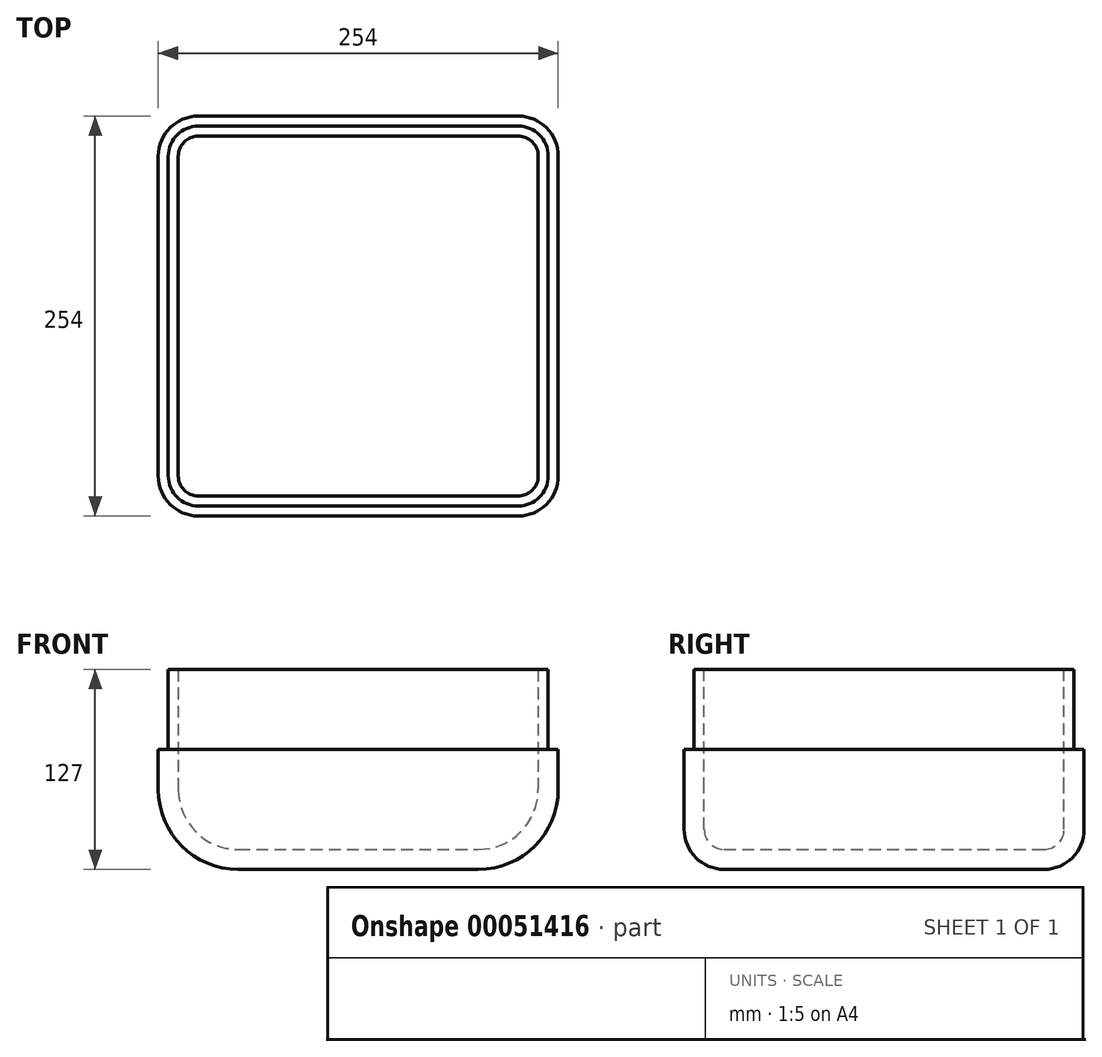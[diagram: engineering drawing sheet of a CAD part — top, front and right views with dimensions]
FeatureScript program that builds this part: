
annotation { "Feature Type Name" : "Feature", "Feature Type Description" : "" }
export const myFeature = defineFeature(function(context is Context, id is Id, definition is map)
    precondition{}
    {
        {
            var Q0;
            Q0=qCreatedBy(makeId("Top.planeOp"),FACE);
            var sketch = newSketch(context, id + "F0", { "sketchPlane" : qUnion([Q0])});
            skLineSegment(sketch, "E0.rect.bottom", {"start": v(-127, 127) * mm, "end": v(127, 127) * mm});
            skLineSegment(sketch, "E0.rect.top", {"start": v(-127, -127) * mm, "end": v(127, -127) * mm});
            skLineSegment(sketch, "E0.rect.left", {"start": v(-127, 127) * mm, "end": v(-127, -127) * mm});
            skLineSegment(sketch, "E0.rect.right", {"start": v(127, 127) * mm, "end": v(127, -127) * mm});
            skPoint(sketch, "E0.rect.middle", {"position": v(0, 0) * mm});
            skSolve(sketch);
        }
        {
            var Q0;
            Q0 = qSketchRegion(id + "F0", true);
            extrude(context, id + "F1", {"entities" : qUnion([Q0]), "depth" : 127 * mm});
        }
        {
            var Q0;
            Q0=makeQuery(id+"F1.opExtrude","SWEPT_EDGE",EDGE,{"disambiguationData":[OSD([sQuery(id+"F0.wireOp",EDGE,"E0.rect.top"),sQuery(id+"F0.wireOp",EDGE,"E0.rect.left")])]});
            var Q1;
            Q1=makeQuery(id+"F1.opExtrude","CAP_EDGE",EDGE,{"disambiguationData":[OSD([sQuery(id+"F0.wireOp",EDGE,"E0.rect.top")])],"isStart":true});
            var Q2;
            Q2=makeQuery(id+"F1.opExtrude","SWEPT_EDGE",EDGE,{"disambiguationData":[OSD([sQuery(id+"F0.wireOp",EDGE,"E0.rect.top"),sQuery(id+"F0.wireOp",EDGE,"E0.rect.right")])]});
            var Q3;
            Q3=makeQuery(id+"F1.opExtrude","SWEPT_EDGE",EDGE,{"disambiguationData":[OSD([sQuery(id+"F0.wireOp",EDGE,"E0.rect.bottom"),sQuery(id+"F0.wireOp",EDGE,"E0.rect.left")])]});
            var Q4;
            Q4=makeQuery(id+"F1.opExtrude","CAP_EDGE",EDGE,{"disambiguationData":[OSD([sQuery(id+"F0.wireOp",EDGE,"E0.rect.bottom")])],"isStart":true});
            var Q5;
            Q5=makeQuery(id+"F1.opExtrude","SWEPT_EDGE",EDGE,{"disambiguationData":[OSD([sQuery(id+"F0.wireOp",EDGE,"E0.rect.bottom"),sQuery(id+"F0.wireOp",EDGE,"E0.rect.right")])]});
            fillet(context, id + "F2", {"entities" : qUnion([Q0, Q1, Q2, Q3, Q4, Q5]), "radius" : 25.4 * mm, "tangentPropagation" : true, "allowEdgeOverflow" : false});
        }
        {
            var Q0;
            Q0=makeQuery(id+"F1.opExtrude","CAP_EDGE",EDGE,{"disambiguationData":[OSD([sQuery(id+"F0.wireOp",EDGE,"E0.rect.left")])],"isStart":true});
            var Q1;
            Q1=makeQuery(id+"F1.opExtrude","CAP_EDGE",EDGE,{"disambiguationData":[OSD([sQuery(id+"F0.wireOp",EDGE,"E0.rect.right")])],"isStart":true});
            fillet(context, id + "F3", {"entities" : qUnion([Q0, Q1]), "radius" : 50.8 * mm, "tangentPropagation" : true, "allowEdgeOverflow" : false});
        }
        {
            var Q0;
            Q0=makeQuery(id+"F1.opExtrude","CAP_FACE",FACE,{"disambiguationData":[OSD([sQuery(id+"F0.wireOp",EDGE,"E0.rect.bottom"),sQuery(id+"F0.wireOp",EDGE,"E0.rect.top"),sQuery(id+"F0.wireOp",EDGE,"E0.rect.left"),sQuery(id+"F0.wireOp",EDGE,"E0.rect.right")])],"isStart":false});
            shell(context, id + "F4", {"entities" : qUnion([Q0]), "thickness" : 12.7 * mm});
        }
        {
            var Q0;
            Q0=makeQuery(id+"F1.opExtrude","CAP_FACE",FACE,{"disambiguationData":[OSD([sQuery(id+"F0.wireOp",EDGE,"E0.rect.bottom"),sQuery(id+"F0.wireOp",EDGE,"E0.rect.top"),sQuery(id+"F0.wireOp",EDGE,"E0.rect.left"),sQuery(id+"F0.wireOp",EDGE,"E0.rect.right")])],"isStart":false});
            var sketch = newSketch(context, id + "F5", { "sketchPlane" : qUnion([Q0])});
            skArc(sketch, "E1.0", {"start": v(-101.6, 120.65) * mm, "mid": v(-115.07, 115.07) * mm, "end": v(-120.65, 101.6) * mm});
            skLineSegment(sketch, "E2.0", {"start": v(-101.6, 120.65) * mm, "end": v(101.6, 120.65) * mm});
            skArc(sketch, "E2.1", {"start": v(120.65, 101.6) * mm, "mid": v(115.07, 115.07) * mm, "end": v(101.6, 120.65) * mm});
            skLineSegment(sketch, "E2.2", {"start": v(120.65, 101.6) * mm, "end": v(120.65, -101.6) * mm});
            skLineSegment(sketch, "E2.3", {"start": v(-120.65, 101.6) * mm, "end": v(-120.65, -101.6) * mm});
            skArc(sketch, "E2.4", {"start": v(-120.65, -101.6) * mm, "mid": v(-115.07, -115.07) * mm, "end": v(-101.6, -120.65) * mm});
            skLineSegment(sketch, "E2.5", {"start": v(-101.6, -120.65) * mm, "end": v(101.6, -120.65) * mm});
            skArc(sketch, "E2.6", {"start": v(101.6, -120.65) * mm, "mid": v(115.07, -115.07) * mm, "end": v(120.65, -101.6) * mm});
            skLineSegment(sketch, "E3.0", {"start": v(-127, 101.6) * mm, "end": v(-127, -101.6) * mm});
            skArc(sketch, "E4.0", {"start": v(-101.6, 127) * mm, "mid": v(-119.56, 119.56) * mm, "end": v(-127, 101.6) * mm});
            skLineSegment(sketch, "E5.0", {"start": v(-101.6, 127) * mm, "end": v(101.6, 127) * mm});
            skArc(sketch, "E6.0", {"start": v(127, 101.6) * mm, "mid": v(119.56, 119.56) * mm, "end": v(101.6, 127) * mm});
            skLineSegment(sketch, "E7.0", {"start": v(127, 101.6) * mm, "end": v(127, -101.6) * mm});
            skArc(sketch, "E8.0", {"start": v(101.6, -127) * mm, "mid": v(119.56, -119.56) * mm, "end": v(127, -101.6) * mm});
            skLineSegment(sketch, "E9.0", {"start": v(-101.6, -127) * mm, "end": v(101.6, -127) * mm});
            skArc(sketch, "E10.0", {"start": v(-127, -101.6) * mm, "mid": v(-119.56, -119.56) * mm, "end": v(-101.6, -127) * mm});
            skSolve(sketch);
        }
        {
            var Q0;
            Q0 = qSketchRegion(id + "F5", true);
            extrude(context, id + "F6", {"entities" : qUnion([Q0]), "operationType" : NewBodyOperationType.REMOVE, "oppositeDirection" : true, "depth" : 50.8 * mm});
        }
    });
